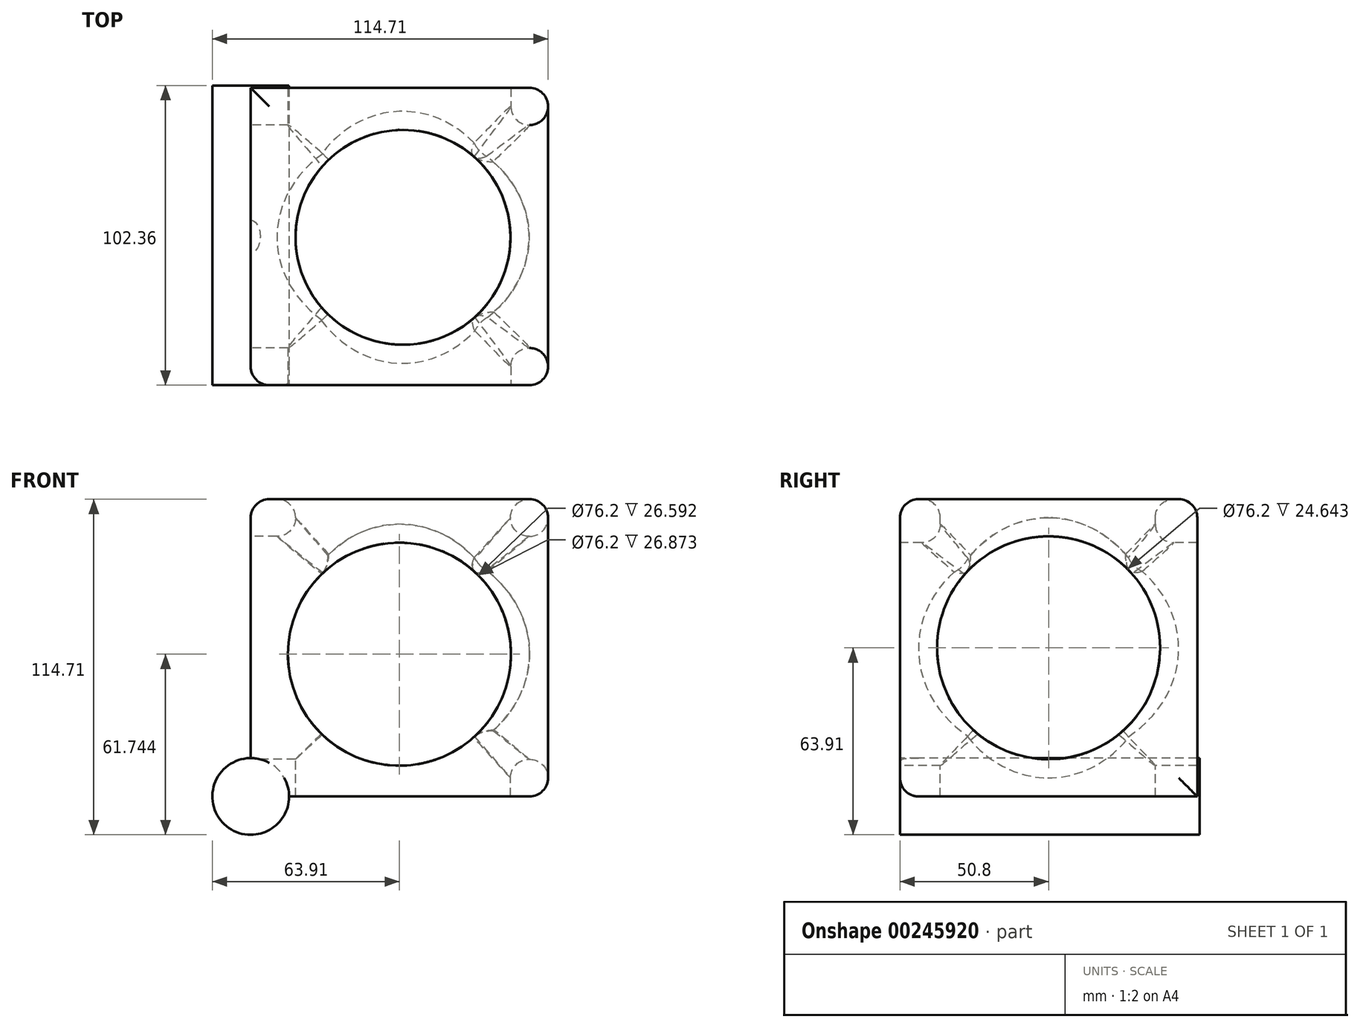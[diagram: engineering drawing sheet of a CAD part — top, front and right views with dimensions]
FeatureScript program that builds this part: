
annotation { "Feature Type Name" : "Feature", "Feature Type Description" : "" }
export const myFeature = defineFeature(function(context is Context, id is Id, definition is map)
    precondition{}
    {
        {
            var Q0;
            Q0=qCreatedBy(makeId("Front.planeOp"),FACE);
            var sketch = newSketch(context, id + "F0", { "sketchPlane" : qUnion([Q0])});
            skLineSegment(sketch, "E0", {"start": v(0, 0) * mm, "end": v(101.6, 0) * mm});
            skLineSegment(sketch, "E1", {"start": v(101.6, 0) * mm, "end": v(101.6, 101.6) * mm});
            skLineSegment(sketch, "E2", {"start": v(101.6, 101.6) * mm, "end": v(0, 101.6) * mm});
            skLineSegment(sketch, "E3", {"start": v(0, 101.6) * mm, "end": v(0, 0) * mm});
            skSolve(sketch);
        }
        {
            var Q0;
            Q0=makeQuery(id+"F0.imprint","IMPRINT",FACE,{"disambiguationData":[TD([[makeQuery(id+"F0.imprint","IMPRINT",EDGE,{"derivedFrom":sQuery(id+"F0.wireOp",EDGE,"E0")}),1.0]])]});
            extrude(context, id + "F1", {"entities" : qUnion([Q0]), "depth" : 101.6 * mm});
        }
        {
            var Q0;
            Q0=makeQuery(id+"F1.opExtrude","SWEPT_FACE",FACE,{"disambiguationData":[OSD([sQuery(id+"F0.wireOp",EDGE,"E2")])]});
            var sketch = newSketch(context, id + "F2", { "sketchPlane" : qUnion([Q0])});
            skSolve(sketch);
        }
        {
            var Q0;
            Q0=makeQuery(id+"F1.opExtrude","CAP_FACE",FACE,{"disambiguationData":[OSD([sQuery(id+"F0.wireOp",EDGE,"E0"),sQuery(id+"F0.wireOp",EDGE,"E1"),sQuery(id+"F0.wireOp",EDGE,"E2"),sQuery(id+"F0.wireOp",EDGE,"E3")])],"isStart":false});
            var sketch = newSketch(context, id + "F3", { "sketchPlane" : qUnion([Q0])});
            skPoint(sketch, "E4.center.orphan", {"position": v(50.8, 50.8) * mm});
            skCircle(sketch, "E5", {"center": v(50.8, 48.63) * mm, "radius": 38.1 * mm});
            skSolve(sketch);
        }
        {
            var Q0;
            Q0=makeQuery(id+"F3.imprint","IMPRINT",FACE,{"disambiguationData":[TD([[makeQuery(id+"F3.imprint","IMPRINT",EDGE,{"derivedFrom":sQuery(id+"F3.wireOp",EDGE,"E5")}),1.0]])]});
            extrude(context, id + "F4", {"entities" : qUnion([Q0]), "operationType" : NewBodyOperationType.REMOVE, "oppositeDirection" : true, "depth" : 101.6 * mm});
        }
        {
            var Q0;
            Q0=makeQuery(id+"F1.opExtrude","SWEPT_FACE",FACE,{"disambiguationData":[OSD([sQuery(id+"F0.wireOp",EDGE,"E3")])]});
            var sketch = newSketch(context, id + "F5", { "sketchPlane" : qUnion([Q0])});
            skCircle(sketch, "E6", {"center": v(50.8, 50.8) * mm, "radius": 38.1 * mm});
            skSolve(sketch);
        }
        {
            var Q0;
            Q0=makeQuery(id+"F5.imprint","IMPRINT",FACE,{"disambiguationData":[TD([[makeQuery(id+"F5.imprint","IMPRINT",EDGE,{"derivedFrom":sQuery(id+"F5.wireOp",EDGE,"E6")}),1.0]])]});
            extrude(context, id + "F6", {"entities" : qUnion([Q0]), "operationType" : NewBodyOperationType.REMOVE, "oppositeDirection" : true, "depth" : 101.6 * mm});
        }
        {
            var Q0;
            {var subQ0=sQuery(id+"F0.wireOp",EDGE,"E2");Q0=makeQuery(id+"F2.imprint","IMPRINT",FACE,{"disambiguationData":[TD([[makeQuery(id+"F2.imprint","IMPRINT",EDGE,{"derivedFrom":makeQuery(id+"F1.opExtrude","CAP_EDGE",EDGE,{"disambiguationData":[OSD([subQ0])],"isStart":true})}),1.0]])]});}
            var sketch = newSketch(context, id + "F7", { "sketchPlane" : qUnion([Q0])});
            skCircle(sketch, "E7", {"center": v(52.02, -51.08) * mm, "radius": 36.72 * mm});
            skSolve(sketch);
        }
        {
            var Q0;
            Q0 = qSketchRegion(id + "F7", true);
            extrude(context, id + "F8", {"entities" : qUnion([Q0]), "operationType" : NewBodyOperationType.REMOVE, "oppositeDirection" : true, "depth" : 101.6 * mm});
        }
        {
            var Q0;
            Q0=makeQuery(id+"F1.opExtrude","CAP_EDGE",EDGE,{"disambiguationData":[OSD([sQuery(id+"F0.wireOp",EDGE,"E2")])],"isStart":false});
            var Q1;
            Q1=makeQuery(id+"F1.opExtrude","CAP_EDGE",EDGE,{"disambiguationData":[OSD([sQuery(id+"F0.wireOp",EDGE,"E1")])],"isStart":false});
            var Q2;
            Q2=makeQuery(id+"F1.opExtrude","CAP_EDGE",EDGE,{"disambiguationData":[OSD([sQuery(id+"F0.wireOp",EDGE,"E3")])],"isStart":false});
            var Q3;
            Q3=makeQuery(id+"F1.opExtrude","CAP_EDGE",EDGE,{"disambiguationData":[OSD([sQuery(id+"F0.wireOp",EDGE,"E0")])],"isStart":false});
            var Q4;
            Q4=makeQuery(id+"F8.boolean.opBoolean","SPLIT",FACE,{"disambiguationData":[TD([makeQuery(id+"F1.opExtrude","SWEPT_FACE",FACE,{"disambiguationData":[OSD([sQuery(id+"F0.wireOp",EDGE,"E1")])]})])],"derivedFrom":makeQuery(id+"F6.boolean.opBoolean","COPY",FACE,{"derivedFrom":makeQuery(id+"F6.opExtrude","SWEPT_FACE",FACE,{"disambiguationData":[OSD([sQuery(id+"F5.wireOp",EDGE,"E6")])]})})});
            var Q5;
            Q5=makeQuery(id+"F1.opExtrude","SWEPT_EDGE",EDGE,{"disambiguationData":[OSD([sQuery(id+"F0.wireOp",EDGE,"E1"),sQuery(id+"F0.wireOp",EDGE,"E2")])]});
            var Q6;
            Q6=makeQuery(id+"F1.opExtrude","CAP_EDGE",EDGE,{"disambiguationData":[OSD([sQuery(id+"F0.wireOp",EDGE,"E1")])],"isStart":true});
            var Q7;
            Q7=makeQuery(id+"F1.opExtrude","SWEPT_EDGE",EDGE,{"disambiguationData":[OSD([sQuery(id+"F0.wireOp",EDGE,"E0"),sQuery(id+"F0.wireOp",EDGE,"E1")])]});
            var Q8;
            Q8=makeQuery(id+"F4.boolean.opBoolean","COPY",EDGE,{"derivedFrom":makeQuery(id+"F4.opExtrude","CAP_EDGE",EDGE,{"disambiguationData":[OSD([sQuery(id+"F3.wireOp",EDGE,"E5")])],"isStart":true})});
            var Q9;
            Q9=makeQuery(id+"F8.boolean.opBoolean","INTERSECT",EDGE,{"disambiguationData":[OD(1.0)],"derivedFrom":[makeQuery(id+"F4.boolean.opBoolean","COPY",FACE,{"derivedFrom":makeQuery(id+"F4.opExtrude","SWEPT_FACE",FACE,{"disambiguationData":[OSD([sQuery(id+"F3.wireOp",EDGE,"E5")])]})}),makeQuery(id+"F8.opExtrude","SWEPT_FACE",FACE,{"disambiguationData":[OSD([sQuery(id+"F7.wireOp",EDGE,"E7")])]})]});
            var Q10;
            Q10=makeQuery(id+"F8.boolean.opBoolean","INTERSECT",EDGE,{"disambiguationData":[OD(1.0)],"derivedFrom":[makeQuery(id+"F6.boolean.opBoolean","COPY",FACE,{"derivedFrom":makeQuery(id+"F6.opExtrude","SWEPT_FACE",FACE,{"disambiguationData":[OSD([sQuery(id+"F5.wireOp",EDGE,"E6")])]})}),makeQuery(id+"F8.opExtrude","SWEPT_FACE",FACE,{"disambiguationData":[OSD([sQuery(id+"F7.wireOp",EDGE,"E7")])]})]});
            var Q11;
            Q11=makeQuery(id+"F6.boolean.opBoolean","COPY",EDGE,{"derivedFrom":makeQuery(id+"F6.opExtrude","CAP_EDGE",EDGE,{"disambiguationData":[OSD([sQuery(id+"F5.wireOp",EDGE,"E6")])],"isStart":true})});
            var Q12;
            Q12=makeQuery(id+"F8.boolean.opBoolean","COPY",FACE,{"disambiguationData":[TD([makeQuery(id+"F1.opExtrude","SWEPT_FACE",FACE,{"disambiguationData":[OSD([sQuery(id+"F0.wireOp",EDGE,"E2")])]})])],"derivedFrom":makeQuery(id+"F8.opExtrude","SWEPT_FACE",FACE,{"disambiguationData":[OSD([sQuery(id+"F7.wireOp",EDGE,"E7")])]})});
            var Q13;
            Q13=makeQuery(id+"F1.opExtrude","SWEPT_EDGE",EDGE,{"disambiguationData":[OSD([sQuery(id+"F0.wireOp",EDGE,"E2"),sQuery(id+"F0.wireOp",EDGE,"E3")])]});
            var Q14;
            Q14=makeQuery(id+"F1.opExtrude","CAP_EDGE",EDGE,{"disambiguationData":[OSD([sQuery(id+"F0.wireOp",EDGE,"E2")])],"isStart":true});
            var Q15;
            Q15=makeQuery(id+"F4.boolean.opBoolean","COPY",EDGE,{"derivedFrom":makeQuery(id+"F4.opExtrude","CAP_EDGE",EDGE,{"disambiguationData":[OSD([sQuery(id+"F3.wireOp",EDGE,"E5")])],"isStart":false})});
            var Q16;
            Q16=makeQuery(id+"F8.boolean.opBoolean","COPY",EDGE,{"derivedFrom":makeQuery(id+"F8.opExtrude","CAP_EDGE",EDGE,{"disambiguationData":[OSD([sQuery(id+"F7.wireOp",EDGE,"E7")])],"isStart":false})});
            var Q17;
            Q17=makeQuery(id+"F8.boolean.opBoolean","INTERSECT",EDGE,{"disambiguationData":[OD(3.0)],"derivedFrom":[makeQuery(id+"F4.boolean.opBoolean","COPY",FACE,{"derivedFrom":makeQuery(id+"F4.opExtrude","SWEPT_FACE",FACE,{"disambiguationData":[OSD([sQuery(id+"F3.wireOp",EDGE,"E5")])]})}),makeQuery(id+"F8.opExtrude","SWEPT_FACE",FACE,{"disambiguationData":[OSD([sQuery(id+"F7.wireOp",EDGE,"E7")])]})]});
            fillet(context, id + "F9", {"entities" : qUnion([Q0, Q1, Q2, Q3, Q4, Q5, Q6, Q7, Q8, Q9, Q10, Q11, Q12, Q13, Q14, Q15, Q16, Q17]), "radius" : 6.35 * mm, "tangentPropagation" : true, "allowEdgeOverflow" : false});
        }
        {
            var Q0;
            Q0=qCreatedBy(makeId("Front.planeOp"),FACE);
            cPlane(context, id + "F10", {"entities" : qUnion([Q0]), "cplaneType" : CPlaneType.OFFSET, "offset" : 101.6 * mm, "width" : 152.4 * mm, "height" : 152.4 * mm});
        }
        {
            var Q0;
            Q0=qCreatedBy(id+"F10.planeOp",FACE);
            var sketch = newSketch(context, id + "F11", { "sketchPlane" : qUnion([Q0])});
            skCircle(sketch, "E8", {"center": v(0, 0) * mm, "radius": 13.1 * mm});
            skSolve(sketch);
        }
        {
            var Q0;
            Q0=makeQuery(id+"F11.imprint","IMPRINT",FACE,{"disambiguationData":[TD([[makeQuery(id+"F11.imprint","IMPRINT",EDGE,{"derivedFrom":sQuery(id+"F11.wireOp",EDGE,"E8")}),1.0]])]});
            extrude(context, id + "F12", {"entities" : qUnion([Q0]), "operationType" : NewBodyOperationType.ADD, "oppositeDirection" : true, "depth" : 102.36 * mm});
        }
    });
